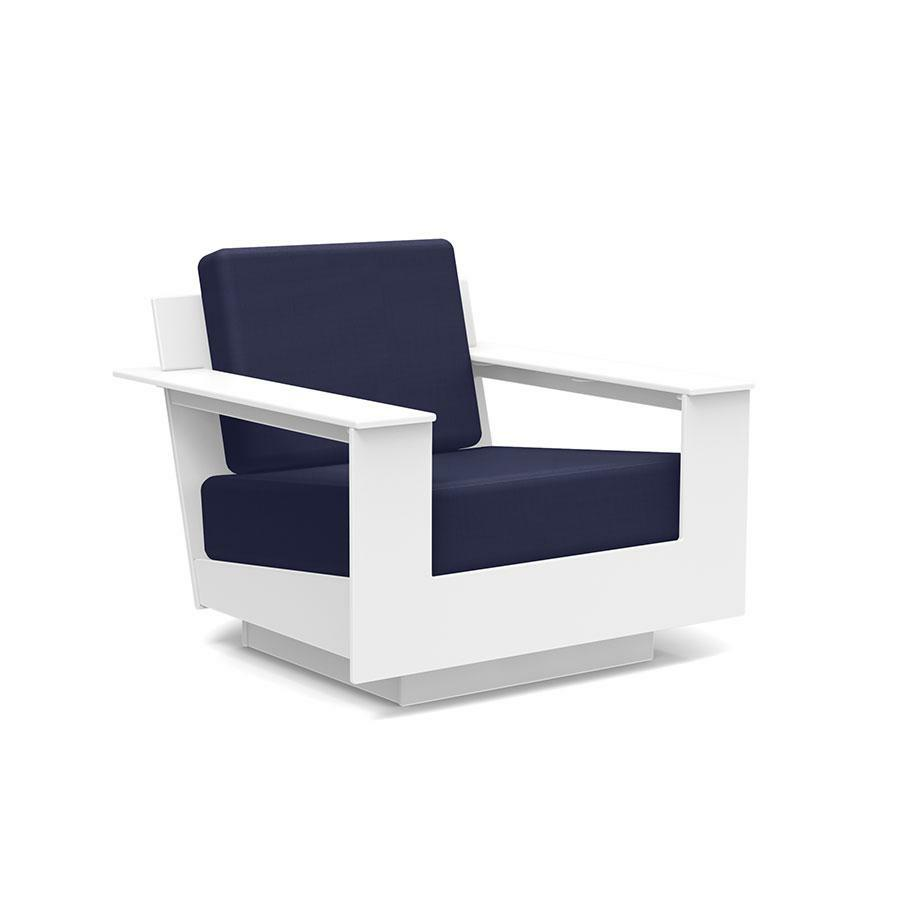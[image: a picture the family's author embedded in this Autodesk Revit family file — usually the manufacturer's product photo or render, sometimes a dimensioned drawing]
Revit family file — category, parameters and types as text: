
# Revit family: Lollygagger Nisswa Lounge Chair
name_source: partatom
category: Furniture
revit_build: Autodesk Revit 2016 (Build: 20150220_1215(x64)
units: mm (PartAtom-declared; Revit-internal decimal feet)

## family parameters
Always vertical = No
Cut with Voids When Loaded = No
OmniClass Number = 23.40.20.00
OmniClass Title = General Furniture and Specialties
Room Calculation Point = No
Shared = No
Work Plane-Based = No

## types (10) — shared parameters
Height = 28 1/8"
Length = 33"
Manufacturer = Loll
Radio = 1"
Sunbrella Back2 = Jockey Red - Loll Design
Thick = 1/2"
Type Image = Nisswa Lounge Chair.jpg
URL = https://lolldesigns.com
Width = 31 19/32"

## per-type parameters (varying)
| type | Finish Material |
| Loll-Black | Loll-White |
| Loll-Sunset | Loll-Sunset |
| Loll-Chocolate | Loll-Chocolate |
| Loll-Sky | Loll-Sky |
| Loll-Apple | Loll-Apple |
| Loll-Leaf | Loll-Leaf |
| Loll-Charcoal | Loll-Charcoal |
| Loll-Navy Blue | Loll-Navy Blue |
| Loll-White | Loll-White |
| Loll-Driftwood | Loll-Driftwood |

## geometry (parser evidence)
native form markers: Blend x2, Sweep x2
no freeform markers — native parametric forms only
